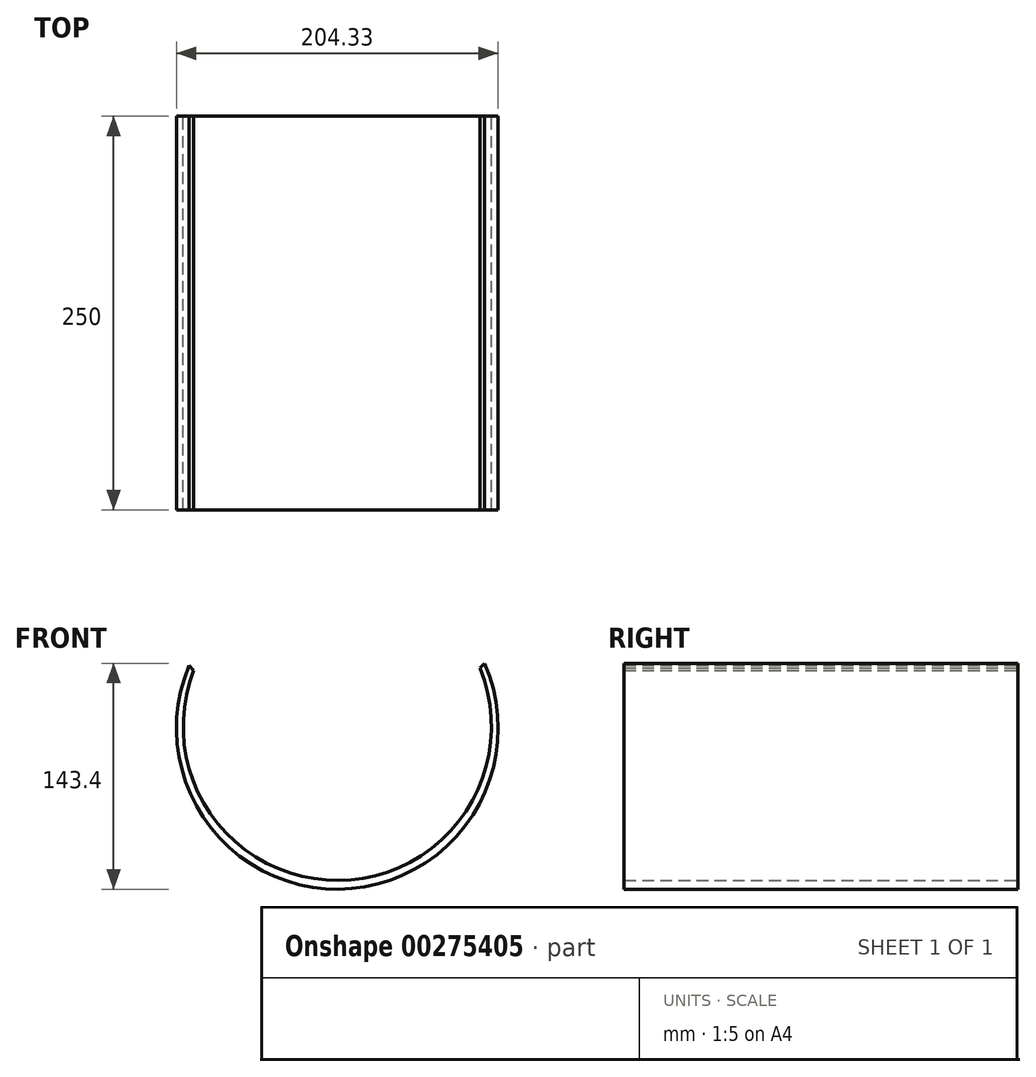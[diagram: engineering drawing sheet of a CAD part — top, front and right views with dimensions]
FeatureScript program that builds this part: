
annotation { "Feature Type Name" : "Feature", "Feature Type Description" : "" }
export const myFeature = defineFeature(function(context is Context, id is Id, definition is map)
    precondition{}
    {
        {
            var Q0;
            Q0=qCreatedBy(makeId("Front.planeOp"),FACE);
            var sketch = newSketch(context, id + "F0", { "sketchPlane" : qUnion([Q0])});
            skPoint(sketch, "E0.start.orphan", {"position": v(-188.83, 58.93) * mm});
            skArc(sketch, "E1", {"start": v(-141.56, 44.33) * mm, "mid": v(-57.85, -117.63) * mm, "end": v(23.05, 45.76) * mm});
            skArc(sketch, "E2", {"start": v(-139.32, 41.33) * mm, "mid": v(-57.85, -112.06) * mm, "end": v(20.89, 42.76) * mm});
            skLineSegment(sketch, "E3", {"start": v(-152.82, 24.33) * mm, "end": v(-149.92, 21.33) * mm});
            skLineSegment(sketch, "E4", {"start": v(31.92, 22.76) * mm, "end": v(34.74, 25.76) * mm});
            skLineSegment(sketch, "E5", {"start": v(-141.56, 44.33) * mm, "end": v(-139.32, 41.33) * mm});
            skLineSegment(sketch, "E6", {"start": v(20.89, 42.76) * mm, "end": v(23.05, 45.76) * mm});
            skSolve(sketch);
        }
        {
            var Q0;
            {var subQ0=sQuery(id+"F0.wireOp",EDGE,"E3");Q0=makeQuery(id+"F0.imprint","IMPRINT",FACE,{"disambiguationData":[TD([[makeQuery(id+"F0.imprint","IMPRINT",EDGE,{"derivedFrom":subQ0}),-1.0]])]});}
            extrude(context, id + "F1", {"entities" : qUnion([Q0]), "depth" : 250 * mm, "offsetDistance" : 25 * mm});
        }
    });
